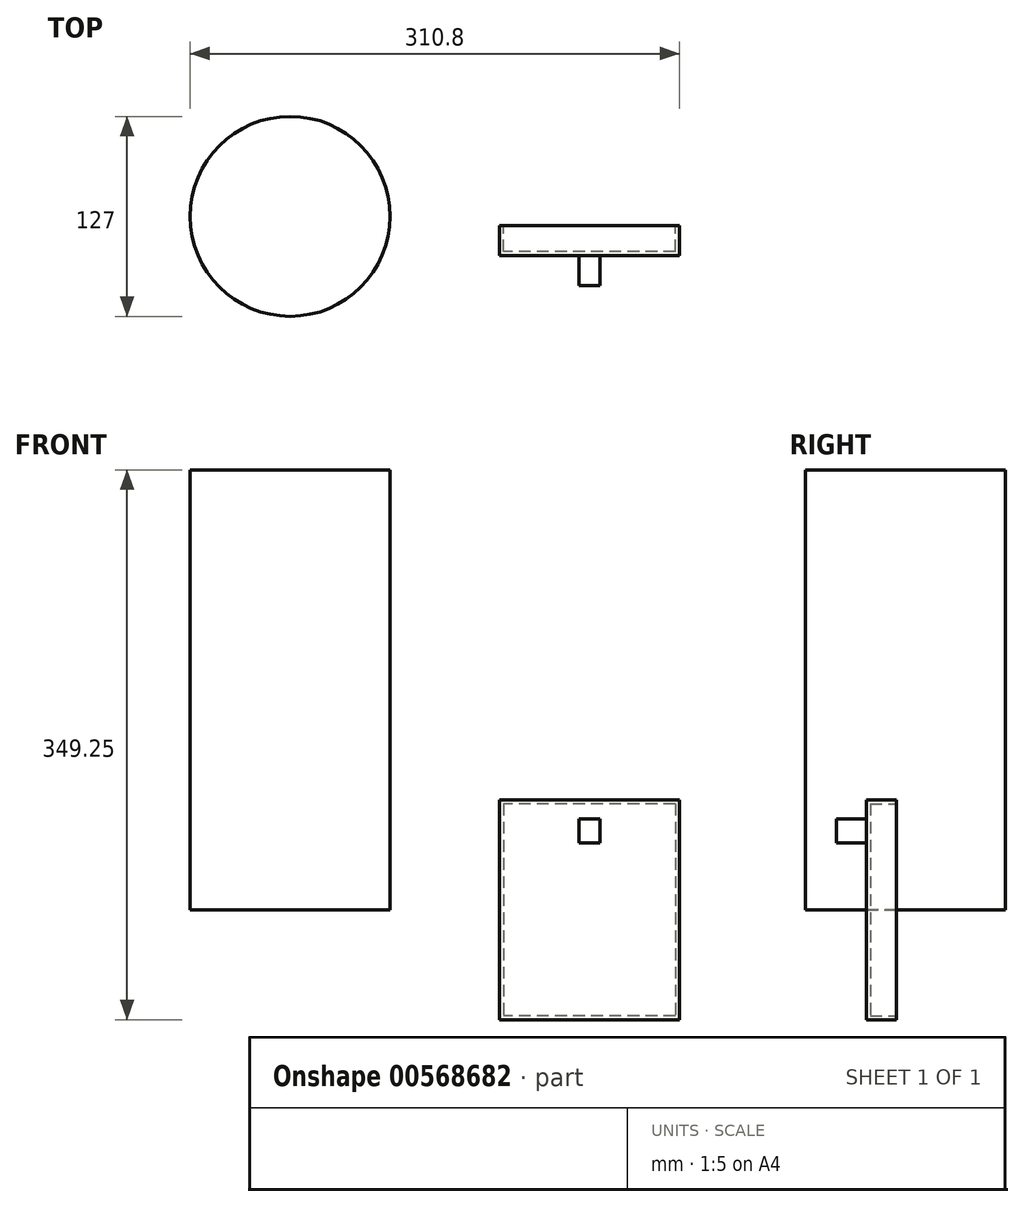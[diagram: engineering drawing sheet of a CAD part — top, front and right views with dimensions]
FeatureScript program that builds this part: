
annotation { "Feature Type Name" : "Feature", "Feature Type Description" : "" }
export const myFeature = defineFeature(function(context is Context, id is Id, definition is map)
    precondition{}
    {
        {
            var Q0;
            Q0=qCreatedBy(makeId("Front.planeOp"),FACE);
            var sketch = newSketch(context, id + "F0", { "sketchPlane" : qUnion([Q0])});
            skLineSegment(sketch, "E0.bottom", {"start": v(57.15, 69.85) * mm, "end": v(-57.15, 69.85) * mm});
            skLineSegment(sketch, "E0.top", {"start": v(57.15, -69.85) * mm, "end": v(-57.15, -69.85) * mm});
            skLineSegment(sketch, "E0.left", {"start": v(57.15, 69.85) * mm, "end": v(57.15, -69.85) * mm});
            skLineSegment(sketch, "E0.right", {"start": v(-57.15, 69.85) * mm, "end": v(-57.15, -69.85) * mm});
            skPoint(sketch, "E0.middle", {"position": v(0, 0) * mm});
            skSolve(sketch);
        }
        {
            var Q0;
            Q0=makeQuery(id+"F0.imprint","IMPRINT",FACE,{"disambiguationData":[TD([[makeQuery(id+"F0.imprint","IMPRINT",EDGE,{"derivedFrom":sQuery(id+"F0.wireOp",EDGE,"E0.bottom")}),1.0]])]});
            extrude(context, id + "F1", {"entities" : qUnion([Q0]), "depth" : 19.05 * mm, "offsetDistance" : 25.4 * mm});
        }
        {
            var Q0;
            Q0=makeQuery(id+"F1.opExtrude","CAP_FACE",FACE,{"disambiguationData":[OSD([sQuery(id+"F0.wireOp",EDGE,"E0.bottom"),sQuery(id+"F0.wireOp",EDGE,"E0.top"),sQuery(id+"F0.wireOp",EDGE,"E0.left"),sQuery(id+"F0.wireOp",EDGE,"E0.right")])],"isStart":true});
            shell(context, id + "F2", {"entities" : qUnion([Q0]), "thickness" : 2.54 * mm});
        }
        {
            var Q0;
            Q0=qCreatedBy(makeId("Front.planeOp"),FACE);
            var sketch = newSketch(context, id + "F3", { "sketchPlane" : qUnion([Q0])});
            skLineSegment(sketch, "E1.bottom", {"start": v(6.7, 42.56) * mm, "end": v(-6.7, 42.56) * mm});
            skLineSegment(sketch, "E1.top", {"start": v(6.7, 57.69) * mm, "end": v(-6.7, 57.69) * mm});
            skLineSegment(sketch, "E1.left", {"start": v(6.7, 42.56) * mm, "end": v(6.7, 57.69) * mm});
            skLineSegment(sketch, "E1.right", {"start": v(-6.7, 42.56) * mm, "end": v(-6.7, 57.69) * mm});
            skPoint(sketch, "E1.middle", {"position": v(0, 50.12) * mm});
            skSolve(sketch);
        }
        {
            var Q0;
            Q0=makeQuery(id+"F3.imprint","IMPRINT",FACE,{"disambiguationData":[TD([[makeQuery(id+"F3.imprint","IMPRINT",EDGE,{"derivedFrom":sQuery(id+"F3.wireOp",EDGE,"E1.bottom")}),-1.0]])]});
            extrude(context, id + "F4", {"entities" : qUnion([Q0]), "operationType" : NewBodyOperationType.ADD, "depth" : 38.1 * mm, "offsetDistance" : 25.4 * mm, "hasSecondDirection" : true, "secondDirectionOppositeDirection" : false, "secondDirectionDepth" : 19.05 * mm});
        }
        {
            var Q0;
            Q0=qCreatedBy(makeId("Top.planeOp"),FACE);
            var sketch = newSketch(context, id + "F5", { "sketchPlane" : qUnion([Q0])});
            skCircle(sketch, "E2", {"center": v(-190.15, 5.81) * mm, "radius": 63.5 * mm});
            skSolve(sketch);
        }
        {
            var Q0;
            Q0 = qSketchRegion(id + "F5", true);
            extrude(context, id + "F6", {"entities" : qUnion([Q0]), "depth" : 279.4 * mm, "offsetDistance" : 25.4 * mm});
        }
    });
